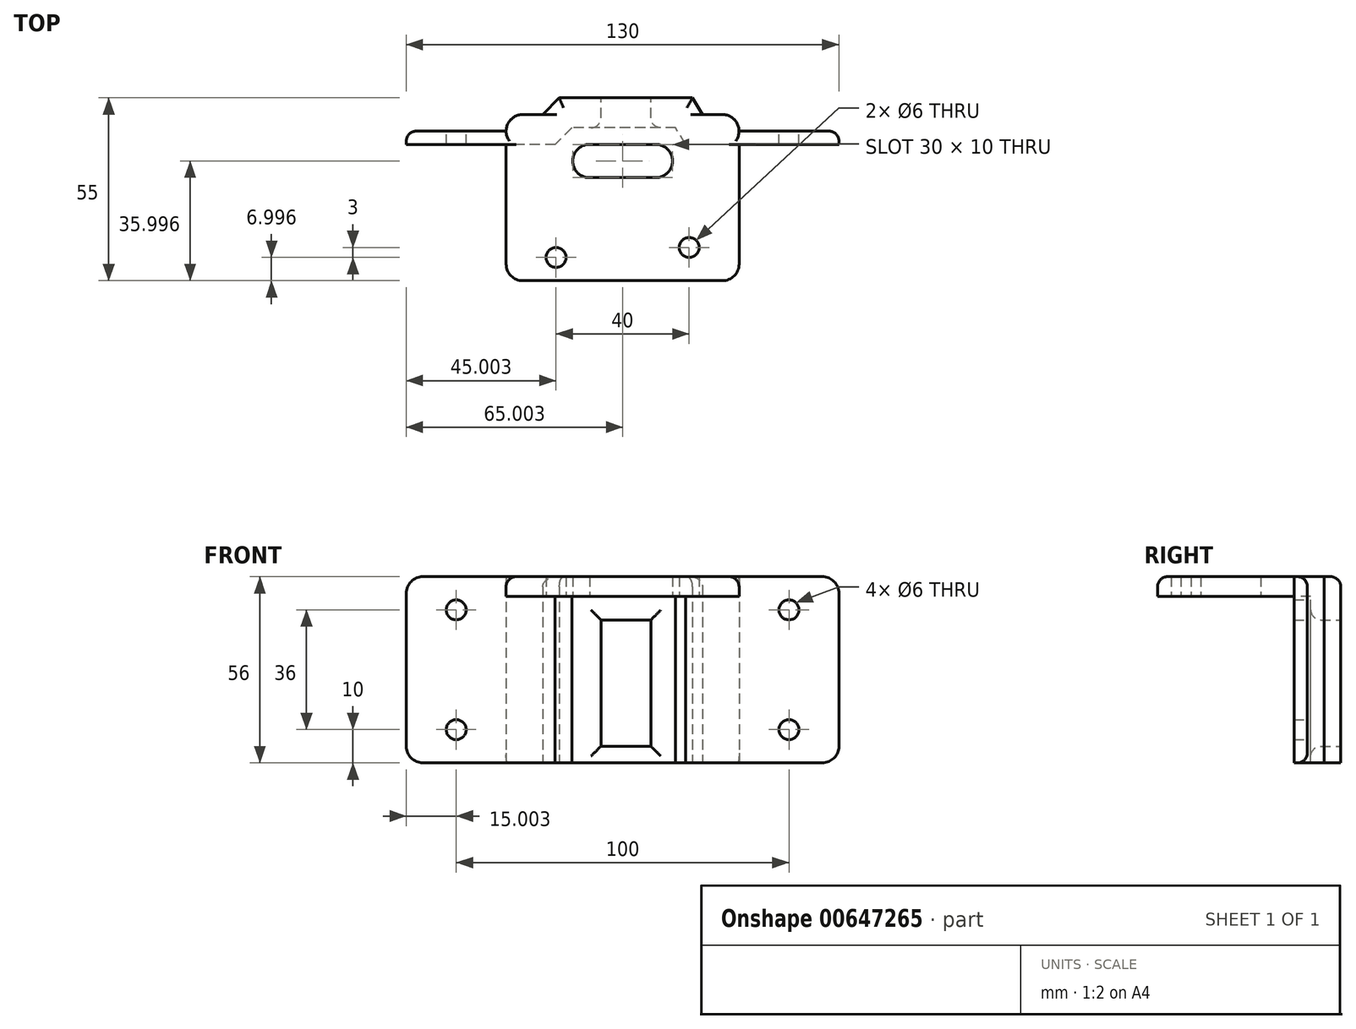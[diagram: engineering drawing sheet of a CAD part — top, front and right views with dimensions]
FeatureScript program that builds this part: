
annotation { "Feature Type Name" : "Feature", "Feature Type Description" : "" }
export const myFeature = defineFeature(function(context is Context, id is Id, definition is map)
    precondition{}
    {
        {
            var Q0;
            Q0=qCreatedBy(makeId("Top.planeOp"),FACE);
            var sketch = newSketch(context, id + "F0", { "sketchPlane" : qUnion([Q0])});
            skLineSegment(sketch, "E0", {"start": v(-36, -23.5) * mm, "end": v(-36, -63.5) * mm});
            skLineSegment(sketch, "E1", {"start": v(-31, -68.5) * mm, "end": v(29, -68.5) * mm});
            skLineSegment(sketch, "E2", {"start": v(34, -63.5) * mm, "end": v(34, -23.5) * mm});
            skLineSegment(sketch, "E3.0", {"start": v(23, -18.5) * mm, "end": v(29, -18.5) * mm});
            skLineSegment(sketch, "E3.1", {"start": v(-31, -18.5) * mm, "end": v(-25, -18.5) * mm});
            skLineSegment(sketch, "E3.2", {"start": v(-20, -13.5) * mm, "end": v(-25, -18.5) * mm});
            skLineSegment(sketch, "E3.3", {"start": v(-20, -13.5) * mm, "end": v(20, -13.5) * mm});
            skLineSegment(sketch, "E3.4", {"start": v(20, -13.5) * mm, "end": v(23, -18.5) * mm});
            skArc(sketch, "E4", {"start": v(-10.93, -27.5) * mm, "mid": v(-16, -32.47) * mm, "end": v(-10.99, -37.5) * mm});
            skArc(sketch, "E5", {"start": v(8.98, -37.5) * mm, "mid": v(14, -32.5) * mm, "end": v(9, -27.5) * mm});
            skPoint(sketch, "E6.visualSharp", {"position": v(34, -18.5) * mm});
            skArc(sketch, "E6.filletArc", {"start": v(34, -23.5) * mm, "mid": v(32.53, -19.96) * mm, "end": v(29, -18.5) * mm});
            skPoint(sketch, "E7.visualSharp", {"position": v(-36, -18.5) * mm});
            skArc(sketch, "E7.filletArc", {"start": v(-31, -18.5) * mm, "mid": v(-34.54, -19.96) * mm, "end": v(-36, -23.5) * mm});
            skPoint(sketch, "E8.visualSharp", {"position": v(-36, -68.5) * mm});
            skArc(sketch, "E8.filletArc", {"start": v(-36, -63.5) * mm, "mid": v(-34.54, -67.03) * mm, "end": v(-31, -68.5) * mm});
            skPoint(sketch, "E9.visualSharp", {"position": v(34, -68.5) * mm});
            skArc(sketch, "E9.filletArc", {"start": v(29, -68.5) * mm, "mid": v(32.53, -67.03) * mm, "end": v(34, -63.5) * mm});
            skLineSegment(sketch, "E10", {"start": v(-11.08, -27.5) * mm, "end": v(9, -27.5) * mm});
            skLineSegment(sketch, "E11", {"start": v(9.01, -37.5) * mm, "end": v(-10.99, -37.5) * mm});
            skCircle(sketch, "E12", {"center": v(-21, -61.5) * mm, "radius": 3 * mm});
            skCircle(sketch, "E13", {"center": v(19, -58.5) * mm, "radius": 3 * mm});
            skSolve(sketch);
        }
        {
            var Q0;
            Q0=makeQuery(id+"F0.imprint","IMPRINT",FACE,{"disambiguationData":[TD([[makeQuery(id+"F0.imprint","IMPRINT",EDGE,{"derivedFrom":sQuery(id+"F0.wireOp",EDGE,"E0")}),1.0]])]});
            extrude(context, id + "F1", {"entities" : qUnion([Q0]), "depth" : 6 * mm, "offsetDistance" : 25 * mm});
        }
        {
            var Q0;
            Q0=makeQuery(id+"F1.opExtrude","CAP_FACE",FACE,{"disambiguationData":[OSD([sQuery(id+"F0.wireOp",EDGE,"E0"),sQuery(id+"F0.wireOp",EDGE,"E1"),sQuery(id+"F0.wireOp",EDGE,"E2"),sQuery(id+"F0.wireOp",EDGE,"E3.0"),sQuery(id+"F0.wireOp",EDGE,"E3.1"),sQuery(id+"F0.wireOp",EDGE,"E3.2"),sQuery(id+"F0.wireOp",EDGE,"E3.3"),sQuery(id+"F0.wireOp",EDGE,"E3.4"),sQuery(id+"F0.wireOp",EDGE,"E4"),sQuery(id+"F0.wireOp",EDGE,"E5"),sQuery(id+"F0.wireOp",EDGE,"E6.filletArc"),sQuery(id+"F0.wireOp",EDGE,"E7.filletArc"),sQuery(id+"F0.wireOp",EDGE,"E8.filletArc"),sQuery(id+"F0.wireOp",EDGE,"E9.filletArc"),sQuery(id+"F0.wireOp",EDGE,"E10"),sQuery(id+"F0.wireOp",EDGE,"E11"),sQuery(id+"F0.wireOp",EDGE,"E12"),sQuery(id+"F0.wireOp",EDGE,"E13")])],"isStart":true});
            var sketch = newSketch(context, id + "F2", { "sketchPlane" : qUnion([Q0])});
            skLineSegment(sketch, "E14", {"start": v(29, 18.5) * mm, "end": v(23, 18.5) * mm});
            skLineSegment(sketch, "E15", {"start": v(23, 18.5) * mm, "end": v(20, 13.5) * mm});
            skLineSegment(sketch, "E16", {"start": v(20, 13.5) * mm, "end": v(-20, 13.5) * mm});
            skLineSegment(sketch, "E17", {"start": v(-20, 13.5) * mm, "end": v(-25, 18.5) * mm});
            skLineSegment(sketch, "E18", {"start": v(-25, 18.5) * mm, "end": v(-31, 18.5) * mm});
            skLineSegment(sketch, "E19.0", {"start": v(-21.28, 27.5) * mm, "end": v(-36, 27.5) * mm});
            skLineSegment(sketch, "E19.1", {"start": v(34, 27.5) * mm, "end": v(17.9, 27.5) * mm});
            skLineSegment(sketch, "E19.2", {"start": v(17.9, 27.5) * mm, "end": v(14.9, 22.5) * mm});
            skLineSegment(sketch, "E19.3", {"start": v(14.9, 22.5) * mm, "end": v(-16.28, 22.5) * mm});
            skLineSegment(sketch, "E19.4", {"start": v(-16.28, 22.5) * mm, "end": v(-21.28, 27.5) * mm});
            skLineSegment(sketch, "E20.0", {"start": v(-17.94, 13.5) * mm, "end": v(17.16, 13.5) * mm});
            skLineSegment(sketch, "E21", {"start": v(-36, 27.5) * mm, "end": v(-36, 23.5) * mm});
            skLineSegment(sketch, "E22", {"start": v(34, 27.5) * mm, "end": v(34, 23.5) * mm});
            skArc(sketch, "E23", {"start": v(29, 18.5) * mm, "mid": v(32.53, 19.96) * mm, "end": v(34, 23.5) * mm});
            skArc(sketch, "E24", {"start": v(-36, 23.5) * mm, "mid": v(-34.54, 19.96) * mm, "end": v(-31, 18.5) * mm});
            skSolve(sketch);
        }
        {
            var Q0;
            Q0 = qSketchRegion(id + "F2", true);
            extrude(context, id + "F3", {"entities" : qUnion([Q0]), "operationType" : NewBodyOperationType.ADD, "depth" : 50 * mm, "offsetDistance" : 25 * mm});
        }
        {
            var Q0;
            Q0=makeQuery(id+"F3.boolean.opBoolean","MERGE",FACE,{"derivedFrom":[makeQuery(id+"F1.opExtrude","SWEPT_FACE",FACE,{"disambiguationData":[OSD([sQuery(id+"F0.wireOp",EDGE,"E3.3")])]}),makeQuery(id+"F3.opExtrude","SWEPT_FACE",FACE,{"disambiguationData":[OSD([sQuery(id+"F2.wireOp",EDGE,"E16"),sQuery(id+"F2.wireOp",EDGE,"E20.0")])]})]});
            var sketch = newSketch(context, id + "F4", { "sketchPlane" : qUnion([Q0])});
            skLineSegment(sketch, "E25.bottom", {"start": v(-7.5, -45) * mm, "end": v(7.5, -45) * mm});
            skLineSegment(sketch, "E25.top", {"start": v(-7.5, -7) * mm, "end": v(7.5, -7) * mm});
            skLineSegment(sketch, "E25.left", {"start": v(-7.5, -45) * mm, "end": v(-7.5, -7) * mm});
            skLineSegment(sketch, "E25.right", {"start": v(7.5, -45) * mm, "end": v(7.5, -7) * mm});
            skSolve(sketch);
        }
        {
            var Q0;
            Q0=makeQuery(id+"F4.imprint","IMPRINT",FACE,{"disambiguationData":[TD([[makeQuery(id+"F4.imprint","IMPRINT",EDGE,{"derivedFrom":sQuery(id+"F4.wireOp",EDGE,"E25.bottom")}),1.0]])]});
            extrude(context, id + "F5", {"entities" : qUnion([Q0]), "operationType" : NewBodyOperationType.REMOVE, "oppositeDirection" : true, "depth" : 25 * mm, "offsetDistance" : 25 * mm});
        }
        {
            var Q0;
            Q0=makeQuery(id+"F3.opExtrude","CAP_FACE",FACE,{"disambiguationData":[OSD([sQuery(id+"F2.wireOp",EDGE,"E14"),sQuery(id+"F2.wireOp",EDGE,"E15"),sQuery(id+"F2.wireOp",EDGE,"E16"),sQuery(id+"F2.wireOp",EDGE,"E17"),sQuery(id+"F2.wireOp",EDGE,"E18"),sQuery(id+"F2.wireOp",EDGE,"E19.0"),sQuery(id+"F2.wireOp",EDGE,"E19.1"),sQuery(id+"F2.wireOp",EDGE,"E19.2"),sQuery(id+"F2.wireOp",EDGE,"E19.3"),sQuery(id+"F2.wireOp",EDGE,"E19.4"),sQuery(id+"F2.wireOp",EDGE,"E20.0"),sQuery(id+"F2.wireOp",EDGE,"E21"),sQuery(id+"F2.wireOp",EDGE,"E22"),sQuery(id+"F2.wireOp",EDGE,"E23"),sQuery(id+"F2.wireOp",EDGE,"E24")])],"isStart":false});
            var sketch = newSketch(context, id + "F6", { "sketchPlane" : qUnion([Q0])});
            skLineSegment(sketch, "E26", {"start": v(34, 27.5) * mm, "end": v(64, 27.5) * mm});
            skLineSegment(sketch, "E27", {"start": v(64, 27.5) * mm, "end": v(64, 23.5) * mm});
            skLineSegment(sketch, "E28", {"start": v(64, 23.5) * mm, "end": v(34, 23.5) * mm});
            skLineSegment(sketch, "E29", {"start": v(34, 23.5) * mm, "end": v(34, 27.5) * mm});
            skLineSegment(sketch, "E30.bottom", {"start": v(-36, 27.5) * mm, "end": v(-66, 27.5) * mm});
            skLineSegment(sketch, "E30.top", {"start": v(-36, 23.5) * mm, "end": v(-66, 23.5) * mm});
            skLineSegment(sketch, "E30.left", {"start": v(-36, 27.5) * mm, "end": v(-36, 23.5) * mm});
            skLineSegment(sketch, "E30.right", {"start": v(-66, 27.5) * mm, "end": v(-66, 23.5) * mm});
            skSolve(sketch);
        }
        {
            var Q0;
            Q0=makeQuery(id+"F6.imprint","IMPRINT",FACE,{"disambiguationData":[TD([[makeQuery(id+"F6.imprint","IMPRINT",EDGE,{"derivedFrom":sQuery(id+"F6.wireOp",EDGE,"E26")}),-1.0]])]});
            var Q1;
            Q1=makeQuery(id+"F6.imprint","IMPRINT",FACE,{"disambiguationData":[TD([[makeQuery(id+"F6.imprint","IMPRINT",EDGE,{"derivedFrom":sQuery(id+"F6.wireOp",EDGE,"E30.bottom")}),1.0]])]});
            extrude(context, id + "F7", {"entities" : qUnion([Q0, Q1]), "operationType" : NewBodyOperationType.ADD, "oppositeDirection" : true, "depth" : 56 * mm, "offsetDistance" : 25 * mm});
        }
        {
            var Q0;
            Q0=makeQuery(id+"F7.opExtrude","SWEPT_FACE",FACE,{"disambiguationData":[OSD([sQuery(id+"F6.wireOp",EDGE,"E28")])]});
            var sketch = newSketch(context, id + "F8", { "sketchPlane" : qUnion([Q0])});
            skCircle(sketch, "E31", {"center": v(-49, -4) * mm, "radius": 3 * mm});
            skCircle(sketch, "E32", {"center": v(-49, -40) * mm, "radius": 3 * mm});
            skCircle(sketch, "E33", {"center": v(51, -4) * mm, "radius": 3 * mm});
            skCircle(sketch, "E34", {"center": v(51, -40) * mm, "radius": 3 * mm});
            skSolve(sketch);
        }
        {
            var Q0;
            Q0=makeQuery(id+"F8.imprint","IMPRINT",FACE,{"disambiguationData":[TD([[makeQuery(id+"F8.imprint","IMPRINT",EDGE,{"derivedFrom":sQuery(id+"F8.wireOp",EDGE,"E31")}),1.0]])]});
            var Q1;
            Q1=makeQuery(id+"F8.imprint","IMPRINT",FACE,{"disambiguationData":[TD([[makeQuery(id+"F8.imprint","IMPRINT",EDGE,{"derivedFrom":sQuery(id+"F8.wireOp",EDGE,"E32")}),1.0]])]});
            var Q2;
            Q2=makeQuery(id+"F8.imprint","IMPRINT",FACE,{"disambiguationData":[TD([[makeQuery(id+"F8.imprint","IMPRINT",EDGE,{"derivedFrom":sQuery(id+"F8.wireOp",EDGE,"E33")}),1.0]])]});
            var Q3;
            Q3=makeQuery(id+"F8.imprint","IMPRINT",FACE,{"disambiguationData":[TD([[makeQuery(id+"F8.imprint","IMPRINT",EDGE,{"derivedFrom":sQuery(id+"F8.wireOp",EDGE,"E34")}),1.0]])]});
            extrude(context, id + "F9", {"entities" : qUnion([Q0, Q1, Q2, Q3]), "operationType" : NewBodyOperationType.REMOVE, "oppositeDirection" : true, "depth" : 25 * mm, "offsetDistance" : 25 * mm});
        }
        {
            var Q0;
            Q0=makeQuery(id+"F7.opExtrude","CAP_EDGE",EDGE,{"disambiguationData":[OSD([sQuery(id+"F6.wireOp",EDGE,"E30.right")])],"isStart":false});
            var Q1;
            Q1=makeQuery(id+"F7.opExtrude","CAP_EDGE",EDGE,{"disambiguationData":[OSD([sQuery(id+"F6.wireOp",EDGE,"E27")])],"isStart":false});
            var Q2;
            Q2=makeQuery(id+"F7.opExtrude","CAP_EDGE",EDGE,{"disambiguationData":[OSD([sQuery(id+"F6.wireOp",EDGE,"E30.right")])],"isStart":true});
            var Q3;
            Q3=makeQuery(id+"F7.opExtrude","CAP_EDGE",EDGE,{"disambiguationData":[OSD([sQuery(id+"F6.wireOp",EDGE,"E27")])],"isStart":true});
            fillet(context, id + "F10", {"entities" : qUnion([Q0, Q1, Q2, Q3]), "radius" : 5 * mm, "tangentPropagation" : true, "allowEdgeOverflow" : false});
        }
        {
            var Q0;
            Q0=makeQuery(id+"F5.boolean.opBoolean","COPY",EDGE,{"derivedFrom":makeQuery(id+"F5.opExtrude","CAP_EDGE",EDGE,{"disambiguationData":[OSD([sQuery(id+"F4.wireOp",EDGE,"E25.left")])],"isStart":true})});
            var Q1;
            Q1=makeQuery(id+"F5.boolean.opBoolean","COPY",EDGE,{"derivedFrom":makeQuery(id+"F5.opExtrude","CAP_EDGE",EDGE,{"disambiguationData":[OSD([sQuery(id+"F4.wireOp",EDGE,"E25.top")])],"isStart":true})});
            var Q2;
            Q2=makeQuery(id+"F5.boolean.opBoolean","COPY",EDGE,{"derivedFrom":makeQuery(id+"F5.opExtrude","CAP_EDGE",EDGE,{"disambiguationData":[OSD([sQuery(id+"F4.wireOp",EDGE,"E25.right")])],"isStart":true})});
            var Q3;
            Q3=makeQuery(id+"F5.boolean.opBoolean","COPY",EDGE,{"derivedFrom":makeQuery(id+"F5.opExtrude","CAP_EDGE",EDGE,{"disambiguationData":[OSD([sQuery(id+"F4.wireOp",EDGE,"E25.bottom")])],"isStart":true})});
            var Q4;
            Q4=makeQuery(id+"F5.boolean.opBoolean","INTERSECT",EDGE,{"derivedFrom":[makeQuery(id+"F3.opExtrude","SWEPT_FACE",FACE,{"disambiguationData":[OSD([sQuery(id+"F2.wireOp",EDGE,"E19.3")])]}),makeQuery(id+"F5.opExtrude","SWEPT_FACE",FACE,{"disambiguationData":[OSD([sQuery(id+"F4.wireOp",EDGE,"E25.left")])]})]});
            var Q5;
            Q5=makeQuery(id+"F5.boolean.opBoolean","INTERSECT",EDGE,{"derivedFrom":[makeQuery(id+"F3.opExtrude","SWEPT_FACE",FACE,{"disambiguationData":[OSD([sQuery(id+"F2.wireOp",EDGE,"E19.3")])]}),makeQuery(id+"F5.opExtrude","SWEPT_FACE",FACE,{"disambiguationData":[OSD([sQuery(id+"F4.wireOp",EDGE,"E25.top")])]})]});
            var Q6;
            Q6=makeQuery(id+"F5.boolean.opBoolean","INTERSECT",EDGE,{"derivedFrom":[makeQuery(id+"F3.opExtrude","SWEPT_FACE",FACE,{"disambiguationData":[OSD([sQuery(id+"F2.wireOp",EDGE,"E19.3")])]}),makeQuery(id+"F5.opExtrude","SWEPT_FACE",FACE,{"disambiguationData":[OSD([sQuery(id+"F4.wireOp",EDGE,"E25.right")])]})]});
            var Q7;
            Q7=makeQuery(id+"F5.boolean.opBoolean","INTERSECT",EDGE,{"derivedFrom":[makeQuery(id+"F3.opExtrude","SWEPT_FACE",FACE,{"disambiguationData":[OSD([sQuery(id+"F2.wireOp",EDGE,"E19.3")])]}),makeQuery(id+"F5.opExtrude","SWEPT_FACE",FACE,{"disambiguationData":[OSD([sQuery(id+"F4.wireOp",EDGE,"E25.bottom")])]})]});
            var Q8;
            Q8=makeQuery(id+"F1.opExtrude","CAP_EDGE",EDGE,{"disambiguationData":[OSD([sQuery(id+"F0.wireOp",EDGE,"E0")])],"isStart":false});
            var Q9;
            Q9=makeQuery(id+"F7.opExtrude","CAP_EDGE",EDGE,{"disambiguationData":[OSD([sQuery(id+"F6.wireOp",EDGE,"E28")])],"isStart":false});
            var Q10;
            Q10=makeQuery(id+"F7.opExtrude","CAP_EDGE",EDGE,{"disambiguationData":[OSD([sQuery(id+"F6.wireOp",EDGE,"E30.top")])],"isStart":false});
            var Q11;
            Q11=makeQuery(id+"F1.opExtrude","CAP_EDGE",EDGE,{"disambiguationData":[OSD([sQuery(id+"F0.wireOp",EDGE,"E3.3")])],"isStart":false});
            var Q12;
            Q12=makeQuery(id+"F1.opExtrude","CAP_EDGE",EDGE,{"disambiguationData":[OSD([sQuery(id+"F0.wireOp",EDGE,"E3.2")])],"isStart":false});
            var Q13;
            Q13=makeQuery(id+"F1.opExtrude","CAP_EDGE",EDGE,{"disambiguationData":[OSD([sQuery(id+"F0.wireOp",EDGE,"E3.4")])],"isStart":false});
            fillet(context, id + "F11", {"entities" : qUnion([Q0, Q1, Q2, Q3, Q4, Q5, Q6, Q7, Q8, Q9, Q10, Q11, Q12, Q13]), "radius" : 3 * mm, "tangentPropagation" : true, "allowEdgeOverflow" : false});
        }
    });
